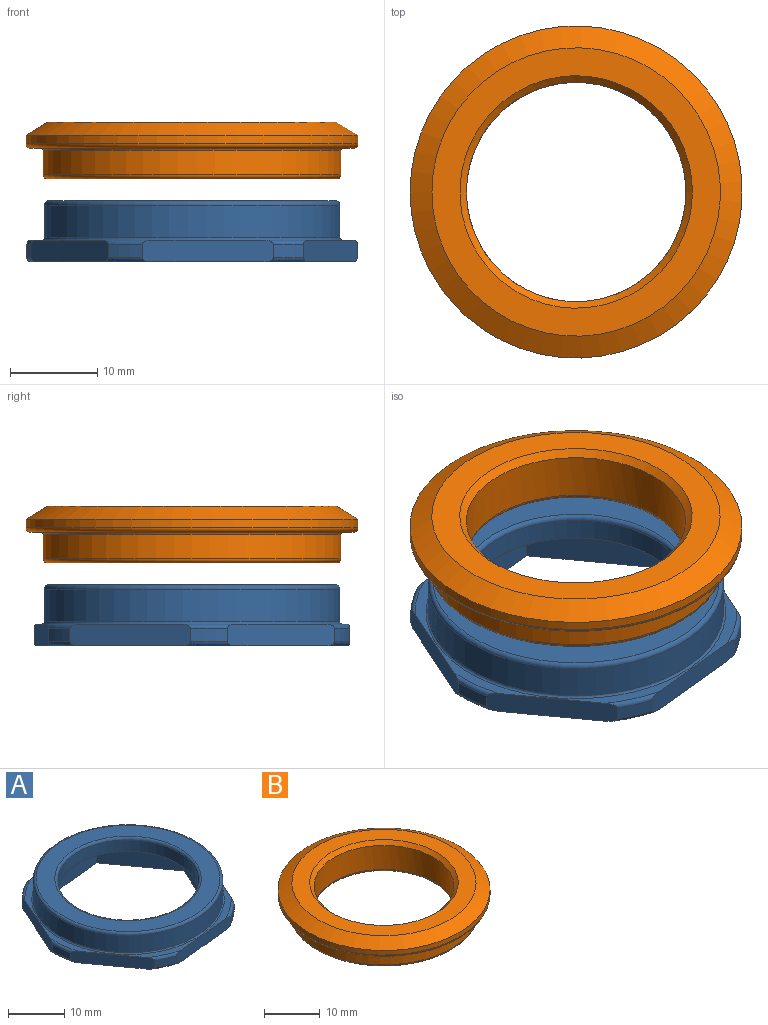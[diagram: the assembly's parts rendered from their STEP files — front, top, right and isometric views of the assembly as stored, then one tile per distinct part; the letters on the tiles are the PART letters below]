
ASSEMBLY  parts=2 mates=1
PART A: 39 faces, bbox 38.4x37.5x7 mm
  f0: torus R=18.4mm, axis (0,0,1), area 4mm2, adj f5,f24,f33,f38
  f1: torus R=18.4mm, axis (0,0,1), area 4mm2, adj f7,f24,f36,f37
  f2: torus R=18.4mm, axis (0,0,1), area 4mm2, adj f8,f24,f35,f36
  f3: torus R=18.4mm, axis (0,0,1), area 4mm2, adj f9,f24,f34,f35
  f4: torus R=18.4mm, axis (0,0,1), area 4mm2, adj f6,f24,f37,f38
  f5: cylinder r=18.9mm len=3.42mm, axis (0,0,1), area 6.3mm2, adj f0,f11,f33,f38
  f6: cylinder r=18.9mm len=3.85mm, axis (0,0,1), area 6.3mm2, adj f4,f12,f37,f38
  f7: cylinder r=18.9mm len=4.2mm, axis (0,0,1), area 6.3mm2, adj f1,f13,f36,f37
  f8: cylinder r=18.9mm len=3.42mm, axis (0,0,1), area 6.3mm2, adj f2,f14,f35,f36
  f9: cylinder r=18.9mm len=3.85mm, axis (0,0,1), area 6.3mm2, adj f3,f15,f34,f35
  f10: cylinder r=18.9mm len=4.2mm, axis (0,0,1), area 6.3mm2, adj f16,f25,f33,f34
  f11: torus R=18.4mm, axis (0,0,1), area 4mm2, adj f5,f17,f33,f38
  f12: torus R=18.4mm, axis (0,0,1), area 4mm2, adj f6,f17,f37,f38
  f13: torus R=18.4mm, axis (0,0,1), area 4mm2, adj f7,f17,f36,f37
  f14: torus R=18.4mm, axis (0,0,1), area 4mm2, adj f8,f17,f35,f36
  f15: torus R=18.4mm, axis (0,0,1), area 4mm2, adj f9,f17,f34,f35
  f16: torus R=18.4mm, axis (0,0,1), area 4mm2, adj f10,f17,f33,f34
  f17: plane 36.8x35.74mm, normal (0,0,-1), area 365.2mm2, adj f11,f12,f13,f14,f15,f16,f27,f28
  f18: cylinder r=12.55mm len=25.1mm, axis (0,0,1), area 197.1mm2, adj f19,f26
  f19: torus R=13.05mm, axis (0,0,1), area 62.8mm2, adj f18,f20
  f20: plane 32.8x32.8mm, normal (0,0,1), area 309.9mm2, adj f19,f21
  f21: torus R=16.4mm, axis (0,0,1), area 82.5mm2, adj f20,f22
  f22: cylinder r=16.9mm len=33.8mm, axis (0,0,1), area 398.2mm2, adj f21,f23
  f23: torus R=17.15mm, axis (0,0,1), area 41.9mm2, adj f22,f24
  f24: plane 36.8x35.74mm, normal (0,0,1), area 85.7mm2, adj f0,f1,f2,f3,f4,f23,f25,f33
  f25: torus R=18.4mm, axis (0,0,1), area 4mm2, adj f10,f24,f33,f34
  f26: plane 31.33x28.76mm, normal (0,0,-1), area 149.7mm2, adj f18,f27,f28,f29,f30,f31,f32
  f27: plane 15.67x4mm, normal (-0.1,0.99,0), area 63mm2, adj f17,f26,f28,f32
  f28: plane 14.38x6.42mm, normal (-0.91,0.41,0), area 63mm2, adj f17,f26,f27,f29
  f29: plane 12.75x9.24mm, normal (-0.81,-0.59,0), area 63mm2, adj f17,f26,f28,f30
  f30: plane 15.67x4mm, normal (0.1,-0.99,0), area 63mm2, adj f17,f26,f29,f31
  f31: plane 14.38x6.42mm, normal (0.91,-0.41,0), area 63mm2, adj f17,f26,f30,f32
  f32: plane 12.75x9.24mm, normal (0.81,0.59,0), area 63mm2, adj f17,f26,f27,f31
  f33: plane 13.81x6.17mm, normal (0.91,-0.41,0), area 37.3mm2, adj f0,f5,f10,f11,f16,f17,f24,f25
  f34: plane 12.25x8.88mm, normal (0.81,0.59,0), area 37.3mm2, adj f3,f9,f10,f15,f16,f17,f24,f25
  f35: plane 15.05x2.5mm, normal (-0.1,0.99,0), area 37.3mm2, adj f2,f3,f8,f9,f14,f15,f17,f24
  f36: plane 13.81x6.17mm, normal (-0.91,0.41,0), area 37.3mm2, adj f1,f2,f7,f8,f13,f14,f17,f24
  f37: plane 12.25x8.88mm, normal (-0.81,-0.59,0), area 37.3mm2, adj f1,f4,f6,f7,f12,f13,f17,f24
  f38: plane 15.05x2.5mm, normal (0.1,-0.99,0), area 37.3mm2, adj f0,f4,f5,f6,f11,f12,f17,f24
PART B: 12 faces, bbox 41.1x41.1x6.5 mm
  f0: cylinder r=17.05mm len=34.1mm, axis (0,0,-1), area 294.6mm2, adj f1,f10
  f1: torus R=16.55mm, axis (0,0,-1), area 83.2mm2, adj f0,f2
  f2: plane 33.1x33.1mm, normal (0,0,-1), area 325.5mm2, adj f1,f3
  f3: torus R=13.05mm, axis (0,0,-1), area 62.8mm2, adj f2,f4
  f4: cylinder r=12.55mm len=25.1mm, axis (0,0,-1), area 414mm2, adj f3,f11
  f5: plane 33x33mm, normal (0,0,1), area 299.6mm2, adj f6,f11
  f6: cone r=19mm half-angle=59deg, axis (0,0,-1), area 325.2mm2, adj f5,f7
  f7: cylinder r=19mm len=38mm, axis (0,0,-1), area 119.4mm2, adj f6,f8
  f8: torus R=18.5mm, axis (0,0,-1), area 92.9mm2, adj f7,f9
  f9: plane 37x37mm, normal (0,0,-1), area 135mm2, adj f8,f10
  f10: torus R=17.3mm, axis (0,0,-1), area 42.3mm2, adj f0,f9
  f11: cone r=13.3mm half-angle=45deg, axis (0,0,1), area 86.1mm2, adj f4,f5
PLACE A t=(1.69,-3.56,4.52)mm
PLACE B t=(18.59,-3.56,11.52)mm
MATE cylindrical A.f0 <-> B.f0  axis (0,0,1) through (18.59,-3.56,9.02)mm
